# Revit family: Door_Operator-Automatic_Swing-Nabco-Bottomload_Header-Simultaneous_Pair-Outswing
name_source: partatom
category: Doors
revit_build: Autodesk Revit Structure 2012 (Build: 20110309_2315(x64)
units: mm (PartAtom-declared; Revit-internal decimal feet)

## types (4) — shared parameters
Date Last Modified = March 9, 2012
Equipment Abbreviation = ASD
Family Version = 1.0.0
Function = Exterior
Is Void = Yes
Manufacturer = NABCO Entrances Inc.
Model = See Part Number
Model Disclaimer = This model represents a highly customizable product.  Contact NABCO Entrances Inc. for more information
Model ID = 5B5D2153-AC8D-4BF6-8A4A-44646BDFF29A
Product Documentation Link = http://www.nabcoentrances.com
Provide Feedback = https://www.surveymonkey.com
Thickness = 1.75 "
URL = http://www.nabcoentrances.com

## per-type parameters (varying)
| type | Description | Part Description | z Type |
| Narrow Stile, Bottom Load | Automatic Swing, Bottom Load Header, Hydraulic Closer, Simultaneous Outswing, Narrow Stile | Automatic Swing, Bottom Load Header, Hydraulic Closer, Simultaneous Outswing, Narrow Stile | 3 |
| Medium Stile, Bottom Load | Automatic Swing, Bottom Load Header, Hydraulic Closer, Simultaneous Outswing, Medium Stile | Automatic Swing, Bottom Load Header, Hydraulic Closer, Simultaneous Outswing, Medium Stile | 1 |
| Medium Stile, Sideload | Automatic Swing, Sideload Header, Spring Closer, Simultaneous Outswing, Medium Stile | Automatic Swing, Sideload Header, Spring Closer, Simultaneous Outswing, Medium Stile | 2 |
| Narrow Stile, Sideload | Automatic Swing, Sideload Header, Spring Closer, Simultaneous Outswing, Narrow Stile | Automatic Swing, Sideload Header, Spring Closer, Simultaneous Outswing, Narrow Stile | 4 |

## geometry (parser evidence)
native form markers: Blend x4, Sweep x4
no freeform markers — native parametric forms only
